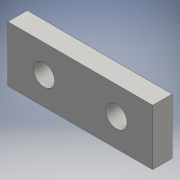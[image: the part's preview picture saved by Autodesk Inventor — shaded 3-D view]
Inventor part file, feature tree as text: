
AUTODESK INVENTOR PART (.ipt)
format: ipt  version: 2016 (Build 200138000, 138)  size: 93,696 bytes
history: native  units: mm
features: extrude x1, sketch x1
ambient origin geometry x8: Origin, YZ Plane, XZ Plane, XY Plane, X Axis, Y Axis, Z Axis, Center Point
bodies: Solid1 (feature_tree)
feature tree (2):
  extrude  "Extrusion1"  Depth=26.0mm
  sketch  "Sketch1"  dims[d0=10.0mm d1=26.0mm d2=3.8mm d4=6.5mm d5=6.5mm d6=13.0mm d7=3.5mm d8=0.0mm]
